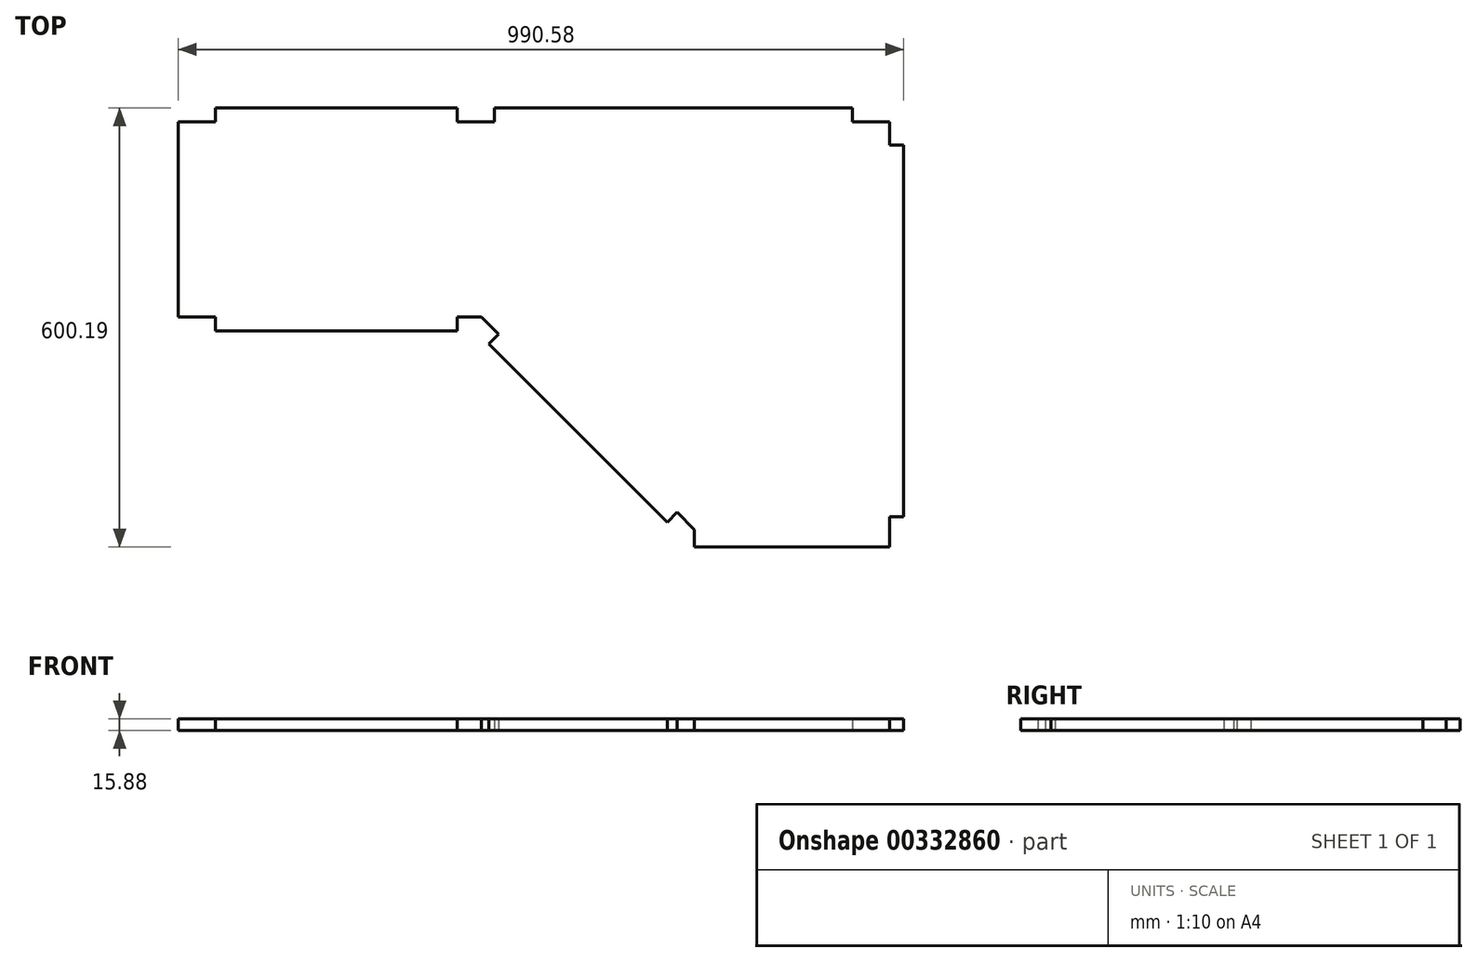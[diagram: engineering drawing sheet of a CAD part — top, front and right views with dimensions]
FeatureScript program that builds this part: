
annotation { "Feature Type Name" : "Feature", "Feature Type Description" : "" }
export const myFeature = defineFeature(function(context is Context, id is Id, definition is map)
    precondition{}
    {
        {
            var Q0;
            Q0=qCreatedBy(makeId("Top.planeOp"),FACE);
            var sketch = newSketch(context, id + "F0", { "sketchPlane" : qUnion([Q0])});
            skLineSegment(sketch, "E0.top", {"start": v(-444.5, 425.45) * mm, "end": v(-114.41, 425.45) * mm});
            skPoint(sketch, "E0.middle", {"position": v(0, 0) * mm});
            skPoint(sketch, "E1.orphan", {"position": v(-495.3, -425.45) * mm});
            skLineSegment(sketch, "E2", {"start": v(172.54, -140.9) * mm, "end": v(-71.05, 102.69) * mm});
            skLineSegment(sketch, "E3", {"start": v(-444.5, 120.65) * mm, "end": v(-114.41, 120.65) * mm});
            skLineSegment(sketch, "E4.top", {"start": v(-495.28, 139.7) * mm, "end": v(-444.5, 139.7) * mm});
            skLineSegment(sketch, "E4.right", {"start": v(-444.5, 120.65) * mm, "end": v(-444.5, 139.7) * mm});
            skLineSegment(sketch, "E5.top", {"start": v(-495.28, 406.4) * mm, "end": v(-444.5, 406.4) * mm});
            skLineSegment(sketch, "E5.right", {"start": v(-444.5, 425.45) * mm, "end": v(-444.5, 406.4) * mm});
            skPoint(sketch, "E6.orphan", {"position": v(-495.3, 425.45) * mm});
            skPoint(sketch, "E7.orphan", {"position": v(495.3, -425.45) * mm});
            skLineSegment(sketch, "E8.top", {"start": v(476.25, 406.4) * mm, "end": v(425.45, 406.4) * mm});
            skLineSegment(sketch, "E8.right", {"start": v(425.45, 425.45) * mm, "end": v(425.45, 406.4) * mm});
            skLineSegment(sketch, "E9.bottom", {"start": v(476.25, 374.65) * mm, "end": v(495.3, 374.65) * mm});
            skLineSegment(sketch, "E9.left", {"start": v(476.25, 374.65) * mm, "end": v(476.25, 406.4) * mm});
            skPoint(sketch, "E10.orphan", {"position": v(495.3, 425.45) * mm});
            skLineSegment(sketch, "E11.top", {"start": v(-114.41, 139.7) * mm, "end": v(-81.12, 139.7) * mm});
            skLineSegment(sketch, "E11.left", {"start": v(-114.41, 120.65) * mm, "end": v(-114.41, 139.7) * mm});
            skLineSegment(sketch, "E12.right", {"start": v(209.55, -174.74) * mm, "end": v(209.55, -150.97) * mm});
            skLineSegment(sketch, "E13", {"start": v(-81.12, 139.7) * mm, "end": v(-57.58, 116.16) * mm});
            skLineSegment(sketch, "E14", {"start": v(172.54, -140.9) * mm, "end": v(186, -127.43) * mm});
            skPoint(sketch, "E15.orphan", {"position": v(190.5, -158.86) * mm});
            skLineSegment(sketch, "E16", {"start": v(-71.05, 102.69) * mm, "end": v(-57.58, 116.16) * mm});
            skPoint(sketch, "E17.orphan", {"position": v(-89.01, 120.65) * mm});
            skLineSegment(sketch, "E18.trimOffspring", {"start": v(186, -127.43) * mm, "end": v(209.55, -150.97) * mm});
            skLineSegment(sketch, "E19.bottom", {"start": v(-114.41, 406.4) * mm, "end": v(-63.61, 406.4) * mm});
            skLineSegment(sketch, "E19.left", {"start": v(-114.41, 406.4) * mm, "end": v(-114.41, 425.45) * mm});
            skLineSegment(sketch, "E19.right", {"start": v(-63.61, 406.4) * mm, "end": v(-63.61, 425.45) * mm});
            skLineSegment(sketch, "E20.top", {"start": v(476.25, -133.46) * mm, "end": v(495.3, -133.46) * mm});
            skLineSegment(sketch, "E20.left", {"start": v(476.25, -174.74) * mm, "end": v(476.25, -133.46) * mm});
            skLineSegment(sketch, "E21.trimOffspring", {"start": v(-63.61, 425.45) * mm, "end": v(425.45, 425.45) * mm});
            skLineSegment(sketch, "E22.trimOffspring", {"start": v(495.3, -133.46) * mm, "end": v(495.3, 374.65) * mm});
            skPoint(sketch, "E23.top.start.orphan", {"position": v(476.25, -374.65) * mm});
            skLineSegment(sketch, "E24.left", {"start": v(-495.28, 139.7) * mm, "end": v(-495.28, 138.44) * mm});
            skLineSegment(sketch, "E25.top", {"start": v(-495.28, 425.45) * mm, "end": v(-495.3, 425.45) * mm});
            skPoint(sketch, "E24.bottom.start.orphan", {"position": v(-1739.88, 406.4) * mm});
            skPoint(sketch, "E26.right.end.orphan", {"position": v(-1739.88, 425.45) * mm});
            skPoint(sketch, "E27.trimOffspring.end.orphan", {"position": v(-1739.88, 120.65) * mm});
            skPoint(sketch, "E28.right.end.orphan", {"position": v(-927.08, 120.65) * mm});
            skLineSegment(sketch, "E29", {"start": v(-495.28, 139.7) * mm, "end": v(-495.28, 406.4) * mm});
            skPoint(sketch, "E30.left.start.orphan", {"position": v(-876.28, 425.45) * mm});
            skPoint(sketch, "E28.left.start.orphan", {"position": v(-876.28, 139.7) * mm});
            skPoint(sketch, "E31.top.end.orphan", {"position": v(-876.28, 120.65) * mm});
            skPoint(sketch, "E31.left.end.orphan", {"position": v(-495.28, 120.65) * mm});
            skLineSegment(sketch, "E32", {"start": v(476.25, -174.74) * mm, "end": v(209.55, -174.74) * mm});
            skPoint(sketch, "E33.orphan", {"position": v(209.55, -184.26) * mm});
            skPoint(sketch, "E34.orphan", {"position": v(476.25, -184.26) * mm});
            skSolve(sketch);
        }
        {
            var Q0;
            Q0=qSketchRegion(id+"F0",true);
            extrude(context, id + "F1", {"entities" : qUnion([Q0]), "depth" : 15.88 * mm});
        }
    });
